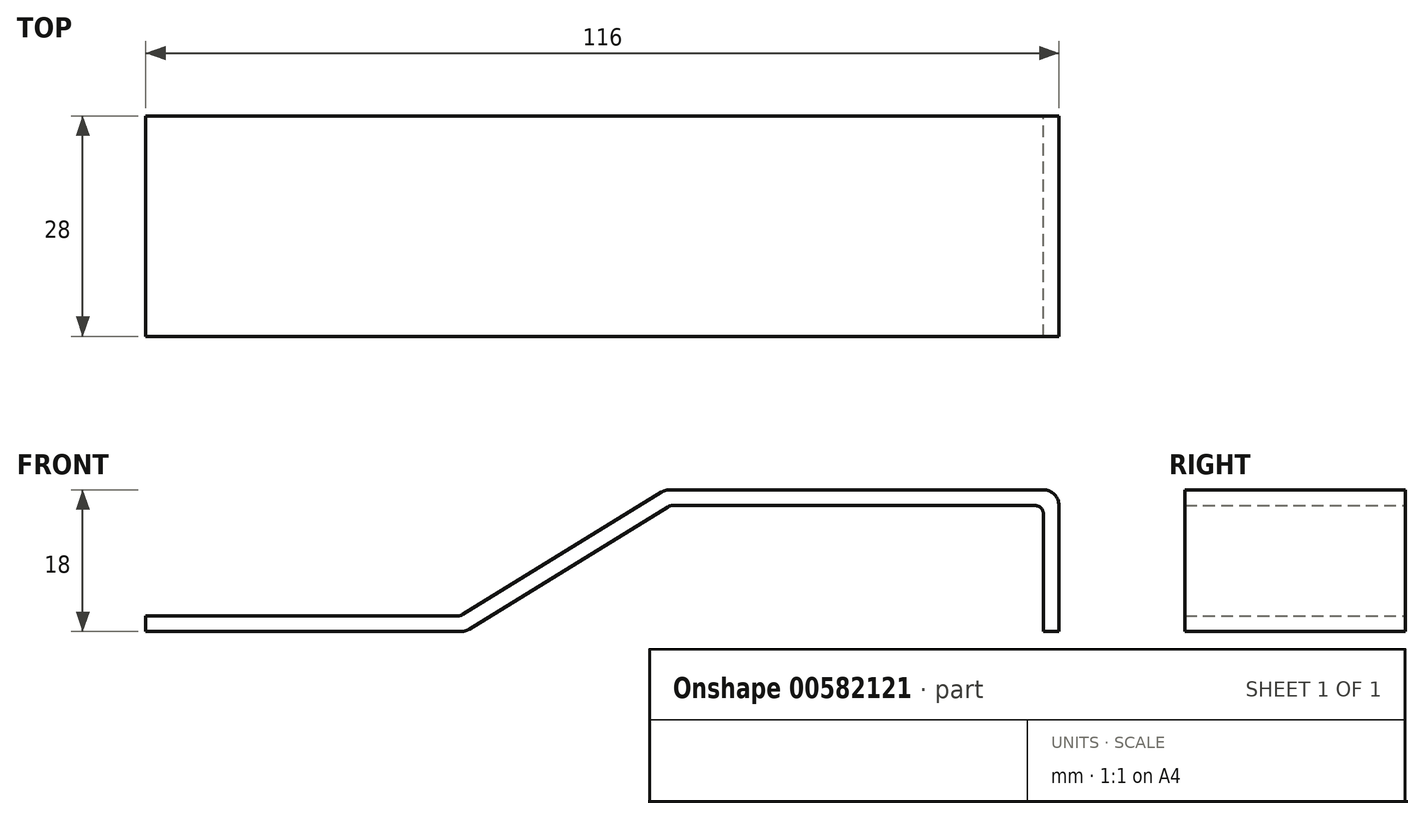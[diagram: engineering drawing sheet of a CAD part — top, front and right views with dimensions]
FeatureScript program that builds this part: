
annotation { "Feature Type Name" : "Feature", "Feature Type Description" : "" }
export const myFeature = defineFeature(function(context is Context, id is Id, definition is map)
    precondition{}
    {
        {
            var Q0;
            Q0=qCreatedBy(makeId("Front.planeOp"),FACE);
            var sketch = newSketch(context, id + "F0", { "sketchPlane" : qUnion([Q0])});
            skLineSegment(sketch, "E0", {"start": v(-51, 0) * mm, "end": v(-51, 2) * mm});
            skLineSegment(sketch, "E1", {"start": v(-51, 2) * mm, "end": v(-11, 2) * mm});
            skLineSegment(sketch, "E2", {"start": v(-11, 2) * mm, "end": v(15, 18) * mm});
            skLineSegment(sketch, "E3", {"start": v(15, 18) * mm, "end": v(65, 18) * mm});
            skLineSegment(sketch, "E4", {"start": v(65, 18) * mm, "end": v(65, 0) * mm});
            skLineSegment(sketch, "E5", {"start": v(65, 0) * mm, "end": v(63, 0) * mm});
            skLineSegment(sketch, "E6", {"start": v(63, 0) * mm, "end": v(63, 16) * mm});
            skLineSegment(sketch, "E7", {"start": v(63, 16) * mm, "end": v(15.57, 16) * mm});
            skLineSegment(sketch, "E8", {"start": v(15.57, 16) * mm, "end": v(-10.43, 0) * mm});
            skLineSegment(sketch, "E9", {"start": v(-10.43, 0) * mm, "end": v(-51, 0) * mm});
            skSolve(sketch);
        }
        {
            var Q0;
            Q0 = qSketchRegion(id + "F0", true);
            extrude(context, id + "F1", {"entities" : qUnion([Q0]), "depth" : 28 * mm, "offsetDistance" : 25 * mm});
        }
        {
            var Q0;
            Q0=makeQuery(id+"F1.opExtrude","SWEPT_EDGE",EDGE,{"disambiguationData":[OSD([sQuery(id+"F0.wireOp",EDGE,"E2"),sQuery(id+"F0.wireOp",EDGE,"E3")])]});
            var Q1;
            Q1=makeQuery(id+"F1.opExtrude","SWEPT_EDGE",EDGE,{"disambiguationData":[OSD([sQuery(id+"F0.wireOp",EDGE,"E3"),sQuery(id+"F0.wireOp",EDGE,"E4")])]});
            var Q2;
            Q2=makeQuery(id+"F1.opExtrude","SWEPT_EDGE",EDGE,{"disambiguationData":[OSD([sQuery(id+"F0.wireOp",EDGE,"E8"),sQuery(id+"F0.wireOp",EDGE,"E9")])]});
            fillet(context, id + "F2", {"entities" : qUnion([Q0, Q1, Q2]), "radius" : 2 * mm, "tangentPropagation" : true, "allowEdgeOverflow" : false});
        }
        {
            var Q0;
            Q0=makeQuery(id+"F1.opExtrude","SWEPT_EDGE",EDGE,{"disambiguationData":[OSD([sQuery(id+"F0.wireOp",EDGE,"E1"),sQuery(id+"F0.wireOp",EDGE,"E2")])]});
            var Q1;
            Q1=makeQuery(id+"F1.opExtrude","SWEPT_EDGE",EDGE,{"disambiguationData":[OSD([sQuery(id+"F0.wireOp",EDGE,"E6"),sQuery(id+"F0.wireOp",EDGE,"E7")])]});
            var Q2;
            Q2=makeQuery(id+"F1.opExtrude","SWEPT_EDGE",EDGE,{"disambiguationData":[OSD([sQuery(id+"F0.wireOp",EDGE,"E7"),sQuery(id+"F0.wireOp",EDGE,"E8")])]});
            fillet(context, id + "F3", {"entities" : qUnion([Q0, Q1, Q2]), "radius" : 1 * mm, "tangentPropagation" : true, "allowEdgeOverflow" : false});
        }
    });
